# Revit family: Lixil-Grohe-Listra-Basin_Mixer_S-106215_0
name_source: partatom
category: Plumbing Fixtures
units: mm (PartAtom-declared; Revit-internal decimal feet)

## family parameters
Cut with Voids When Loaded = No
Enable Cutting in Views = Yes
Host = Face
Maintain Annotation Orientation = No
OmniClass Number = 23.45.55.17
OmniClass Title = Mixing Faucets
Part Type = Normal
Room Calculation Point = No
Round Connector Dimension = Use Diameter
Shared = No

## types (1)
- Listra Basin Mixer, S
    Assembly Code = D2010400
    Brand = Grohe
    CW Connection = Yes
    Collection = Listra
    Default Elevation = 0"
    Depth = 4 5/16"
    Description = Basin Mixer, S
    Finish = Metal - Grohe - Chrome
    HW Connection = Yes
    Horizontal Offset Drain = 6 1/2"
    Keynote = 22 40 00
    Manufacturer = LIXIL
    Model = 106215_0
    Product Documentation Link = https://www.grohe.us
    Product Name = Listra Basin Mixer, S
    Product Page URL = https://www.grohe.us
    URL = https://www.grohe.us
    Vent Connection = No
    Version = 2023 - v1.0a
    Vertical Offset Drain = 1"
    Warranty URL = https://www.grohe.us
    Waste Connection = No
    Width = 2 3/8"

## geometry (parser evidence)
native form markers: Sweep x7
no freeform markers — native parametric forms only
